# Revit family: FORM&REFINE_TREFOIL_TABLE_ROUND_90_OAK
name_source: partatom
category: Arredi
units: mm (PartAtom-declared; Revit-internal decimal feet)

## family parameters
Attiva taglio nelle viste = No
Basato su piano di lavoro = No
Condiviso = No
Numero OmniClass = 23.40.20.00
Origine composizione di rendering = Geometria famiglia
Punto di calcolo locali = No
Sempre verticale = Sì
Taglio con vuoti quando caricato = No
Titolo OmniClass = General Furniture and Specialties

## types (1)
- ROUND_90_OAK
    ACCESSORIES = NN
    AVAILABLE FINISHES = Oak, White Oak
    BIM BADGE = https://bim.archiproducts.com
    COLLECTION = Trefoil
    DEPTH = 900 mm  [stored 2.95276 ft]
    DESIGN = Herman Studio, 2024
    Descrizione = Round dining table with centered four-leg column creating shadow effect, FSC solid oak, Ø90cm, H72.5cm.
    HEIGHT = 725 mm  [stored 2.37861 ft]
    MATERIAL DESCRIPTION = FSC®-certified Solid European Oak
    Modello = Trefoil Round Table Ø90
    PACKAGING = nn
    PRODUCT CODE = 1265
    PRODUCT SHEET = https://www.archiproducts.com
    Produttore = Form & Refine
    Prospetto di default = 0 mm  [stored 0 ft]
    ROUN = Sì
    SEAT HEIGHT = 0 mm  [stored 0 ft]
    SQUARE = No
    STRUCTURE MATERIAL = FORM_&_REFINE_SOLID_OAK_NATURAL_OIL
    TECHNICAL SHEET = https://formandrefine.com
    URL = https://formandrefine.com
    USAGE = indoor
    WARRANTY = 5 years
    WEIGHT = 5.10 kg
    WIDTH = 900 mm  [stored 2.95276 ft]

note: [stored X ft] marks values corroborated as IEEE doubles in the binary element streams (Revit-internal decimal feet)
